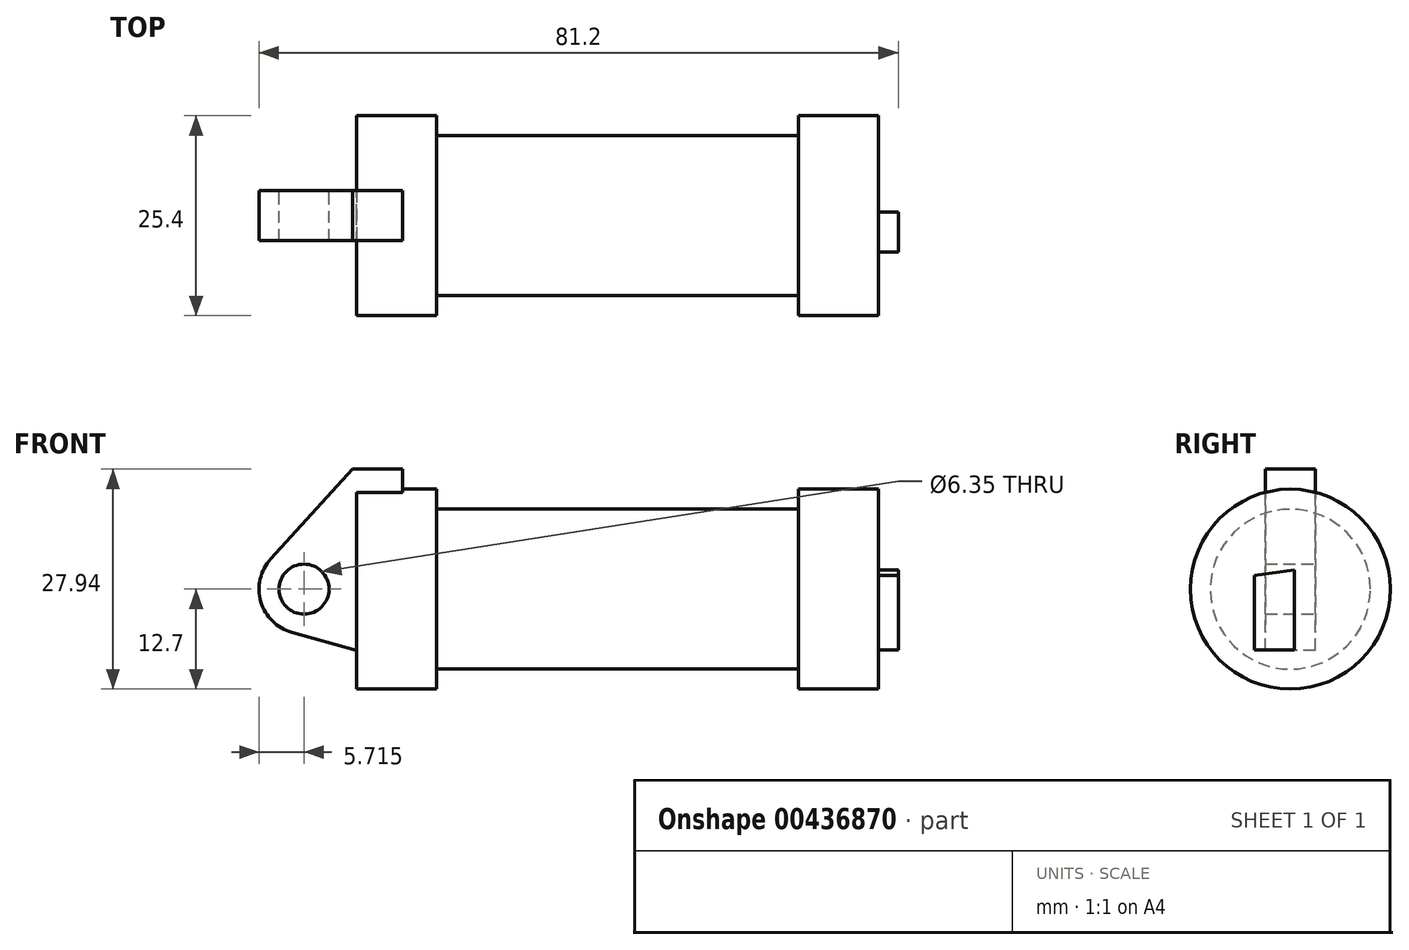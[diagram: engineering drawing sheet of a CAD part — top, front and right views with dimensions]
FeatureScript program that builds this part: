
annotation { "Feature Type Name" : "Feature", "Feature Type Description" : "" }
export const myFeature = defineFeature(function(context is Context, id is Id, definition is map)
    precondition{}
    {
        {
            var Q0;
            Q0=qCreatedBy(makeId("Front.planeOp"),FACE);
            var sketch = newSketch(context, id + "F0", { "sketchPlane" : qUnion([Q0])});
            skLineSegment(sketch, "E0", {"start": v(0, 0) * mm, "end": v(0, 12.7) * mm});
            skLineSegment(sketch, "E1", {"start": v(0, 12.7) * mm, "end": v(10.16, 12.7) * mm});
            skLineSegment(sketch, "E2", {"start": v(10.16, 12.7) * mm, "end": v(10.16, 10.16) * mm});
            skLineSegment(sketch, "E3", {"start": v(10.16, 10.16) * mm, "end": v(56.13, 10.16) * mm});
            skLineSegment(sketch, "E4", {"start": v(56.13, 10.16) * mm, "end": v(56.13, 12.7) * mm});
            skLineSegment(sketch, "E5", {"start": v(56.13, 12.7) * mm, "end": v(66.3, 12.7) * mm});
            skLineSegment(sketch, "E6", {"start": v(66.3, 12.7) * mm, "end": v(66.3, 0) * mm});
            skLineSegment(sketch, "E7", {"start": v(66.3, 0) * mm, "end": v(0, 0) * mm});
            skLineSegment(sketch, "E8", {"start": v(5.84, 15.24) * mm, "end": v(-0.5, 15.24) * mm});
            skLineSegment(sketch, "E9", {"start": v(-0.5, 15.24) * mm, "end": v(-10.88, 3.85) * mm});
            skLineSegment(sketch, "E10", {"start": v(0, 0) * mm, "end": v(-6.65, 0) * mm});
            skCircle(sketch, "E11", {"center": v(-6.65, 0) * mm, "radius": 5.72 * mm});
            skCircle(sketch, "E12", {"center": v(-6.65, 0) * mm, "radius": 3.18 * mm});
            skLineSegment(sketch, "E13", {"start": v(5.84, 15.24) * mm, "end": v(5.84, -9.4) * mm});
            skLineSegment(sketch, "E14", {"start": v(5.84, -9.4) * mm, "end": v(-8.18, -5.5) * mm});
            skLineSegment(sketch, "E15", {"start": v(0, 0) * mm, "end": v(0, -7.78) * mm});
            skSolve(sketch);
        }
        {
            var Q0;
            {var subQ1=sQuery(id+"F0.wireOp",EDGE,"E0");Q0=makeQuery(id+"F0.imprint","IMPRINT",FACE,{"disambiguationData":[TD([[makeQuery(id+"F0.imprint","IMPRINT",EDGE,{"derivedFrom":subQ1}),1.0]])]});}
            var Q1;
            {var subQ5=sQuery(id+"F0.wireOp",EDGE,"E12");Q1=makeQuery(id+"F0.imprint","IMPRINT",FACE,{"disambiguationData":[TD([[makeQuery(id+"F0.imprint","IMPRINT",EDGE,{"derivedFrom":subQ5}),-1.0]])]});}
            var Q2;
            {var subQ0=sQuery(id+"F0.wireOp",EDGE,"E15");Q2=makeQuery(id+"F0.imprint","IMPRINT",FACE,{"disambiguationData":[TD([[makeQuery(id+"F0.imprint","IMPRINT",EDGE,{"derivedFrom":subQ0}),-1.0]])]});}
            var Q3;
            {var subQ0=sQuery(id+"F0.wireOp",EDGE,"E15");Q3=makeQuery(id+"F0.imprint","IMPRINT",FACE,{"disambiguationData":[TD([[makeQuery(id+"F0.imprint","IMPRINT",EDGE,{"derivedFrom":subQ0}),1.0]])]});}
            var Q4;
            {var subQ0=sQuery(id+"F0.wireOp",EDGE,"E0");Q4=makeQuery(id+"F0.imprint","IMPRINT",FACE,{"disambiguationData":[TD([[makeQuery(id+"F0.imprint","IMPRINT",EDGE,{"derivedFrom":subQ0}),-1.0]])]});}
            extrude(context, id + "F1", {"entities" : qUnion([Q0, Q1, Q2, Q3, Q4]), "endBound" : BoundingType.SYMMETRIC, "depth" : 6.35 * mm});
        }
        {
            var Q0;
            {var subQ0=sQuery(id+"F0.wireOp",EDGE,"E2");Q0=makeQuery(id+"F0.imprint","IMPRINT",FACE,{"disambiguationData":[TD([[makeQuery(id+"F0.imprint","IMPRINT",EDGE,{"derivedFrom":subQ0}),-1.0]])]});}
            var Q1;
            {var subQ0=sQuery(id+"F0.wireOp",EDGE,"E0");Q1=makeQuery(id+"F0.imprint","IMPRINT",FACE,{"disambiguationData":[TD([[makeQuery(id+"F0.imprint","IMPRINT",EDGE,{"derivedFrom":subQ0}),-1.0]])]});}
            var Q2;
            Q2=sQuery(id+"F0.wireOp",EDGE,"E7");
            revolve(context, id + "F2", {"operationType" : NewBodyOperationType.ADD, "entities" : qUnion([Q0, Q1]), "axis" : qUnion([Q2]), "revolveType" : RevolveType.FULL});
        }
        {
            var Q0;
            Q0=makeQuery(id+"F2.opRevolve","SWEPT_FACE",FACE,{"disambiguationData":[OSD([sQuery(id+"F0.wireOp",EDGE,"E6")])]});
            var sketch = newSketch(context, id + "F3", { "sketchPlane" : qUnion([Q0])});
            skLineSegment(sketch, "E16", {"start": v(-4.59, 1.77) * mm, "end": v(-4.59, -7.71) * mm});
            skLineSegment(sketch, "E17", {"start": v(-4.59, -7.71) * mm, "end": v(0.5, -7.71) * mm});
            skLineSegment(sketch, "E18", {"start": v(0.5, -7.71) * mm, "end": v(0.5, 2.46) * mm});
            skLineSegment(sketch, "E19", {"start": v(0.5, 2.46) * mm, "end": v(-4.59, 1.77) * mm});
            skSolve(sketch);
        }
        {
            var Q0;
            Q0 = qSketchRegion(id + "F3", true);
            extrude(context, id + "F4", {"entities" : qUnion([Q0]), "operationType" : NewBodyOperationType.ADD, "depth" : 2.54 * mm});
        }
    });
